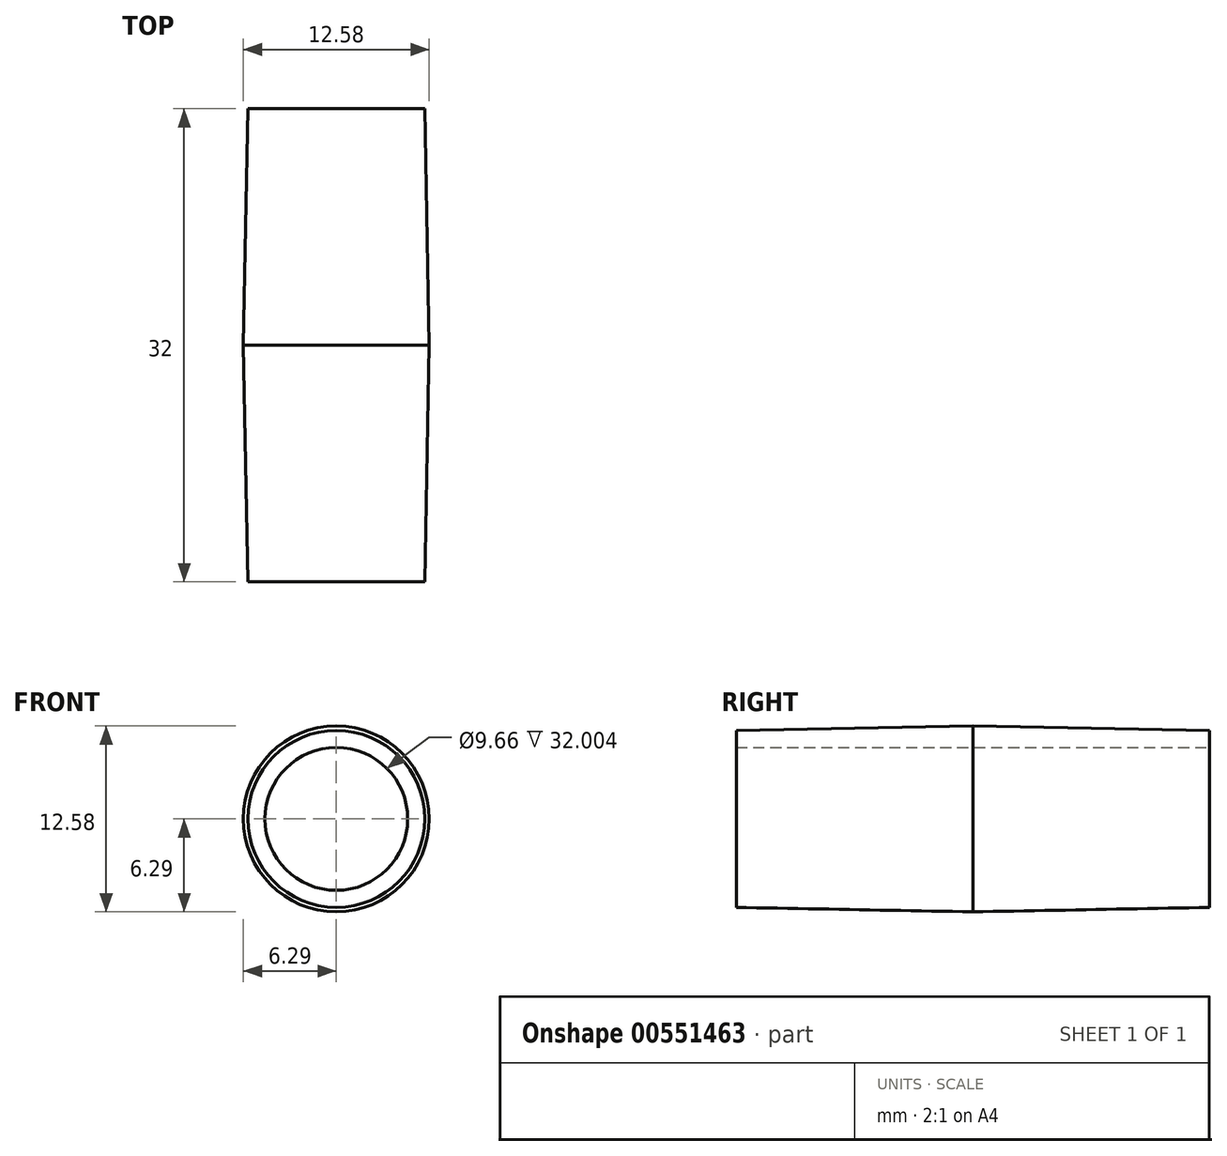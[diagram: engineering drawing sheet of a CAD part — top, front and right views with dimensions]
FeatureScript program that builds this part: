
annotation { "Feature Type Name" : "Feature", "Feature Type Description" : "" }
export const myFeature = defineFeature(function(context is Context, id is Id, definition is map)
    precondition{}
    {
        {
            var Q0;
            Q0=qCreatedBy(makeId("Front.planeOp"),FACE);
            var sketch = newSketch(context, id + "F0", { "sketchPlane" : qUnion([Q0])});
            skCircle(sketch, "E0", {"center": v(0, 0) * mm, "radius": 5.98 * mm});
            skSolve(sketch);
        }
        {
            var Q0;
            Q0=qCreatedBy(makeId("Front.planeOp"),FACE);
            cPlane(context, id + "F1", {"entities" : qUnion([Q0]), "cplaneType" : CPlaneType.OFFSET, "offset" : 16 * mm, "width" : 152.4 * mm, "height" : 152.4 * mm});
        }
        {
            var Q0;
            Q0=qCreatedBy(id+"F1.planeOp",FACE);
            var sketch = newSketch(context, id + "F2", { "sketchPlane" : qUnion([Q0])});
            skCircle(sketch, "E1", {"center": v(0, 0) * mm, "radius": 6.29 * mm});
            skSolve(sketch);
        }
        {
            var Q0;
            Q0=makeQuery(id+"F0.imprint","IMPRINT",FACE,{"disambiguationData":[TD([[makeQuery(id+"F0.imprint","IMPRINT",EDGE,{"derivedFrom":sQuery(id+"F0.wireOp",EDGE,"E0")}),1.0]])]});
            var Q1;
            Q1=makeQuery(id+"F2.imprint","IMPRINT",FACE,{"disambiguationData":[TD([[makeQuery(id+"F2.imprint","IMPRINT",EDGE,{"derivedFrom":sQuery(id+"F2.wireOp",EDGE,"E1")}),1.0]])]});
            loft(context, id + "F3", {"sheetProfilesArray" : [{ "sheetProfileEntities" : qUnion([Q0]) }, { "sheetProfileEntities" : qUnion([Q1]) }]});
        }
        {
            var Q0;
            Q0=makeQuery(id+"F3.opLoft","SWEPT_BODY",BODY,{"disambiguationData":[OSD([makeQuery(id+"F0.imprint","IMPRINT",FACE,{"disambiguationData":[TD([[makeQuery(id+"F0.imprint","IMPRINT",EDGE,{"derivedFrom":sQuery(id+"F0.wireOp",EDGE,"E0")}),1.0]])]}),makeQuery(id+"F2.imprint","IMPRINT",FACE,{"disambiguationData":[TD([[makeQuery(id+"F2.imprint","IMPRINT",EDGE,{"derivedFrom":sQuery(id+"F2.wireOp",EDGE,"E1")}),1.0]])]})])]});
            var Q1;
            Q1=qCreatedBy(id+"F1.planeOp",FACE);
            mirror(context, id + "F4", {"operationType" : NewBodyOperationType.ADD, "entities" : qUnion([Q0]), "mirrorPlane" : qUnion([Q1])});
        }
        {
            var Q0;
            Q0=makeQuery(id+"F3.opLoft","CAP_FACE",FACE,{"disambiguationData":[OSD([makeQuery(id+"F0.imprint","IMPRINT",FACE,{"disambiguationData":[TD([[makeQuery(id+"F0.imprint","IMPRINT",EDGE,{"derivedFrom":sQuery(id+"F0.wireOp",EDGE,"E0")}),1.0]])]})])],"isStart":true});
            var sketch = newSketch(context, id + "F5", { "sketchPlane" : qUnion([Q0])});
            skCircle(sketch, "E2", {"center": v(0, 0) * mm, "radius": 4.83 * mm});
            skSolve(sketch);
        }
        {
            var Q0;
            Q0=makeQuery(id+"F5.imprint","IMPRINT",FACE,{"disambiguationData":[TD([[makeQuery(id+"F5.imprint","IMPRINT",EDGE,{"derivedFrom":sQuery(id+"F5.wireOp",EDGE,"E2")}),1.0]])]});
            extrude(context, id + "F6", {"entities" : qUnion([Q0]), "operationType" : NewBodyOperationType.REMOVE, "oppositeDirection" : true, "depth" : 50.8 * mm, "offsetDistance" : 25.4 * mm});
        }
    });
